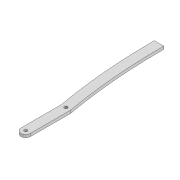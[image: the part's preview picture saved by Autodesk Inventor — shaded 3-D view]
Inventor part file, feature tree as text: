
AUTODESK INVENTOR PART (.ipt)
format: ipt  version: 2022 (Build 260153000, 153)  size: 112,640 bytes
history: native  units: mm
features: extrude x2, sketch x2
ambient origin geometry x8: Origin, YZ Plane, XZ Plane, XY Plane, X Axis, Y Axis, Z Axis, Center Point
bodies: Solid1 (feature_tree)
feature tree (4):
  extrude  "Extrusion1"  Depth=3.3mm
  extrude  "Extrusion2"  Depth=10.0mm
  sketch  "Sketch1"  dims[d0=3.3mm d1=3.3mm]
  sketch  "Sketch2"  dims[d2=10.0mm d3=312.648mm d6=3.0mm d7=0.0mm d10=3.3mm d11=42.6mm d12=3.3mm d13=254.274mm d16=600.0mm d17=600.0mm d18=10.0mm d19=0.0mm]
